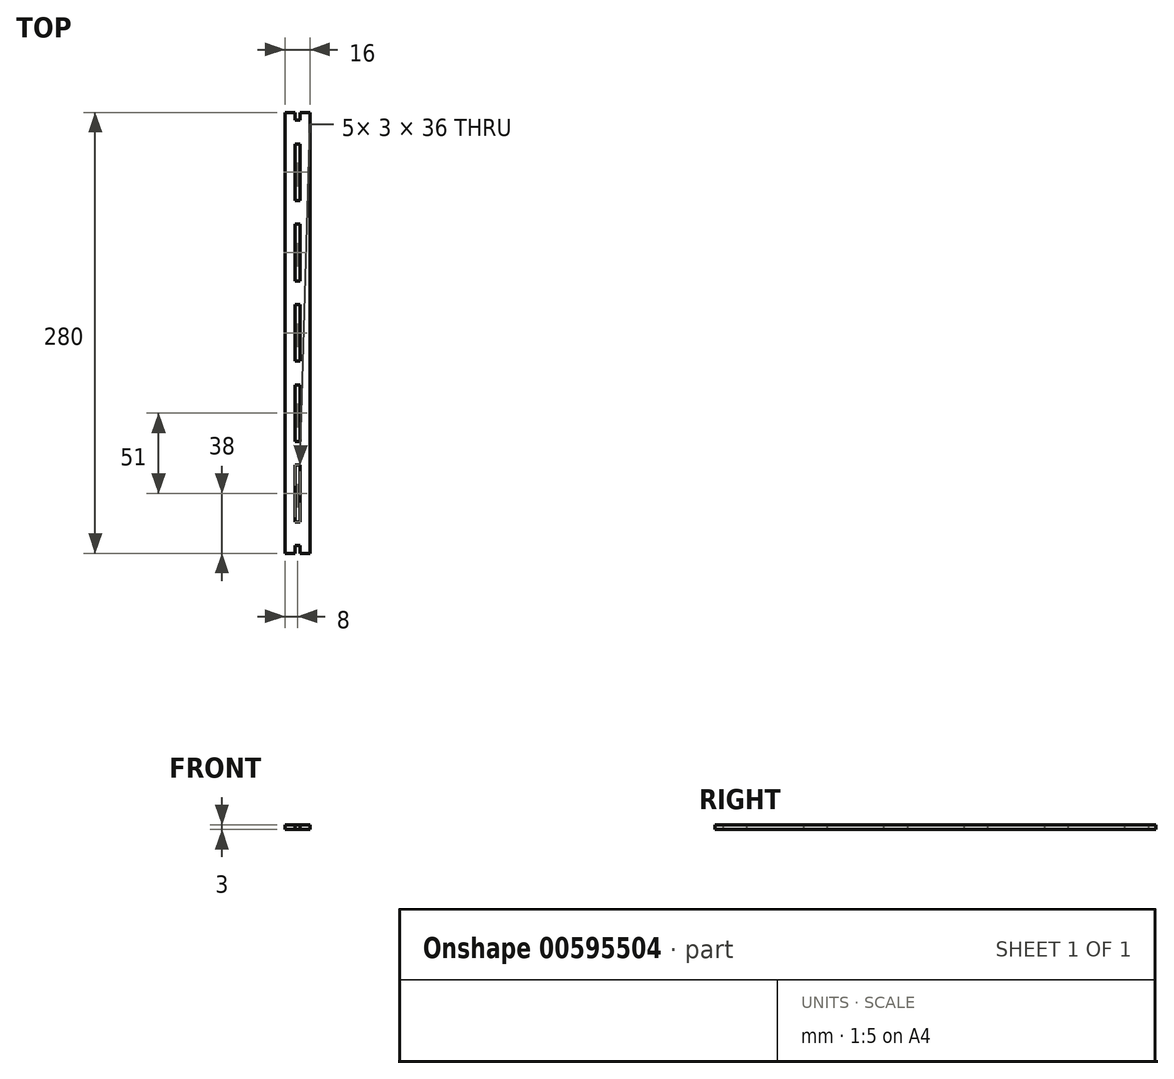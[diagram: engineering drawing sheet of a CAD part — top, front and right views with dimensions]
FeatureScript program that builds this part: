
annotation { "Feature Type Name" : "Feature", "Feature Type Description" : "" }
export const myFeature = defineFeature(function(context is Context, id is Id, definition is map)
    precondition{}
    {
        {
            var Q0;
            Q0=qCreatedBy(makeId("Top.planeOp"),FACE);
            var sketch = newSketch(context, id + "F0", { "sketchPlane" : qUnion([Q0])});
            skLineSegment(sketch, "E0.bottom", {"start": v(-6.5, 0) * mm, "end": v(-9.5, 0) * mm});
            skLineSegment(sketch, "E0.top", {"start": v(-6.5, -270) * mm, "end": v(-9.5, -270) * mm});
            skLineSegment(sketch, "E0.left", {"start": v(0, 0) * mm, "end": v(0, -270) * mm});
            skLineSegment(sketch, "E0.right", {"start": v(-16, 0) * mm, "end": v(-16, -270) * mm});
            skLineSegment(sketch, "E1.bottom", {"start": v(-9.5, -255) * mm, "end": v(-6.5, -255) * mm});
            skLineSegment(sketch, "E1.top", {"start": v(-9.5, -219) * mm, "end": v(-6.5, -219) * mm});
            skLineSegment(sketch, "E1.left", {"start": v(-9.5, -255) * mm, "end": v(-9.5, -219) * mm});
            skLineSegment(sketch, "E1.right", {"start": v(-6.5, -255) * mm, "end": v(-6.5, -219) * mm});
            skLineSegment(sketch, "E2.bottom", {"start": v(-9.5, -204) * mm, "end": v(-6.5, -204) * mm});
            skLineSegment(sketch, "E2.top", {"start": v(-9.5, -168) * mm, "end": v(-6.5, -168) * mm});
            skLineSegment(sketch, "E2.left", {"start": v(-9.5, -204) * mm, "end": v(-9.5, -168) * mm});
            skLineSegment(sketch, "E2.right", {"start": v(-6.5, -204) * mm, "end": v(-6.5, -168) * mm});
            skLineSegment(sketch, "E3.bottom", {"start": v(-9.5, -153) * mm, "end": v(-6.5, -153) * mm});
            skLineSegment(sketch, "E3.top", {"start": v(-9.5, -117) * mm, "end": v(-6.5, -117) * mm});
            skLineSegment(sketch, "E3.left", {"start": v(-9.5, -153) * mm, "end": v(-9.5, -117) * mm});
            skLineSegment(sketch, "E3.right", {"start": v(-6.5, -153) * mm, "end": v(-6.5, -117) * mm});
            skLineSegment(sketch, "E4.bottom", {"start": v(-9.5, -102) * mm, "end": v(-6.5, -102) * mm});
            skLineSegment(sketch, "E4.top", {"start": v(-9.5, -66) * mm, "end": v(-6.5, -66) * mm});
            skLineSegment(sketch, "E4.left", {"start": v(-9.5, -102) * mm, "end": v(-9.5, -66) * mm});
            skLineSegment(sketch, "E4.right", {"start": v(-6.5, -102) * mm, "end": v(-6.5, -66) * mm});
            skLineSegment(sketch, "E5.bottom", {"start": v(-9.5, -51) * mm, "end": v(-6.5, -51) * mm});
            skLineSegment(sketch, "E5.top", {"start": v(-9.5, -15) * mm, "end": v(-6.5, -15) * mm});
            skLineSegment(sketch, "E5.left", {"start": v(-9.5, -51) * mm, "end": v(-9.5, -15) * mm});
            skLineSegment(sketch, "E5.right", {"start": v(-6.5, -51) * mm, "end": v(-6.5, -15) * mm});
            skLineSegment(sketch, "E6", {"start": v(-16, 0) * mm, "end": v(-16, 5) * mm});
            skLineSegment(sketch, "E7", {"start": v(-16, 5) * mm, "end": v(-9.5, 5) * mm});
            skLineSegment(sketch, "E8", {"start": v(-9.5, 5) * mm, "end": v(-9.5, 0) * mm});
            skLineSegment(sketch, "E9", {"start": v(-9.5, 0) * mm, "end": v(-6.5, 0) * mm});
            skLineSegment(sketch, "E10", {"start": v(-6.5, 0) * mm, "end": v(-6.5, 5) * mm});
            skLineSegment(sketch, "E11", {"start": v(-6.5, 5) * mm, "end": v(0, 5) * mm});
            skLineSegment(sketch, "E12", {"start": v(0, 5) * mm, "end": v(0, 0) * mm});
            skLineSegment(sketch, "E13", {"start": v(-16, -270) * mm, "end": v(-16, -275) * mm});
            skLineSegment(sketch, "E14", {"start": v(-16, -275) * mm, "end": v(-9.5, -275) * mm});
            skLineSegment(sketch, "E15", {"start": v(-9.5, -275) * mm, "end": v(-9.5, -270) * mm});
            skLineSegment(sketch, "E16", {"start": v(-9.5, -270) * mm, "end": v(-6.5, -270) * mm});
            skLineSegment(sketch, "E17", {"start": v(-6.5, -270) * mm, "end": v(-6.5, -275) * mm});
            skLineSegment(sketch, "E18", {"start": v(-6.5, -275) * mm, "end": v(0, -275) * mm});
            skLineSegment(sketch, "E19", {"start": v(0, -275) * mm, "end": v(0, -270) * mm});
            skSolve(sketch);
        }
        {
            var Q0;
            Q0=makeQuery(id+"F0.imprint","IMPRINT",FACE,{"disambiguationData":[TD([[makeQuery(id+"F0.imprint","IMPRINT",EDGE,{"derivedFrom":sQuery(id+"F0.wireOp",EDGE,"E0.left")}),-1.0]])]});
            extrude(context, id + "F1", {"entities" : qUnion([Q0]), "depth" : 3 * mm, "offsetDistance" : 25 * mm});
        }
    });
